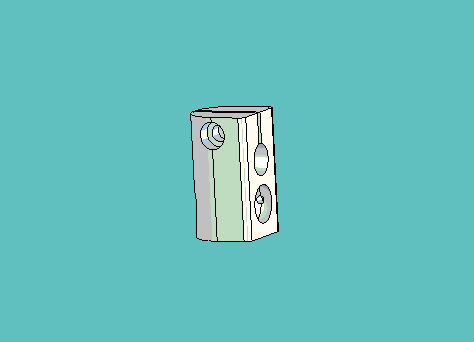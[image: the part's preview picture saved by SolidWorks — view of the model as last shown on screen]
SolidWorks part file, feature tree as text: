
SOLIDWORKS PART (.sldprt)
format: sldprt  version: not decoded by parser v0  size: 622,592 bytes
history: native  units: mm
features: sketch x9, cut_extrude x7, fillet x2, material x1, extrude x1, revolve x1, boolean_combine x1, plane x1 (+11 scaffold rows collapsed)
feature tree (34):
  scaffold x11  (default folders/planes/origin — collapsed)
  material  "Material <not specified>"
  sketch  "Sketch1"  dims[D1=19.05mm]
  extrude  "Extrude1"  Depth=33.3375mm
  sketch  "Sketch2"  dims[c1.D1=3.4544mm c1.D2=2.159mm c1.D6=2.159mm c1.D7=3.4544mm c1.D3=8.7376mm c1.D4=28.3464mm c2.D3=8.7376mm c2.D4=28.3464mm c2.D5=8.7376mm c2.D8=28.3464mm]
  cut_extrude  "Cut-Extrude1"  [1 undecoded]
  sketch  "Sketch3"  dims[c1.D4=12.7mm c1.D1=8.7376mm c1.D2=12.7mm c1.D3=6.35mm c1.D5=7.62mm c1.D6=5.1562mm c2.D2=22.225mm c2.D5=~24.868775mm c2.D1=8.7376mm]
  revolve  "Revolve1"  Angle=360deg
  boolean_combine  "Combine1"
  sketch  "Sketch4"  dims[D1=8.6106mm D2=20.6502mm]
  cut_extrude  "Cut-Extrude2"  [1 undecoded]
  sketch  "Sketch5"  dims[D1=4.4704mm]
  cut_extrude  "Cut-Extrude3"  [1 undecoded]
  plane  "Plane1"  Offset=12.7mm
  sketch  "Sketch6"  dims[D1=7.366mm]
  cut_extrude  "Cut-Extrude4"  Depth=7.9375mm
  sketch  "Sketch7"  dims[D1=~0.79375mm D2=~0.79375mm]
  cut_extrude  "Cut-Extrude5"  Depth=12.7mm
  sketch  "Sketch10"  dims[D1=2.159mm]
  cut_extrude  "Cut-Extrude7"  [1 undecoded]
  sketch  "Sketch12"  dims[D2=2.159mm D1=~15.14602mm]
  cut_extrude  "Cut-Extrude8"  [1 undecoded]
  fillet  "Fillet1"  Radius=1.5875mm
  fillet  "Fillet2"  Radius=9.525mm
decode coverage: 15 of 21 modeling features carry decoded parameters
note: ~ marks probable driven/reference dimensions
note: 5 parameter values undecoded
summary: no parameter record found for 5 features
note: suppression state not decoded; provenance and decode notes live in map.json
